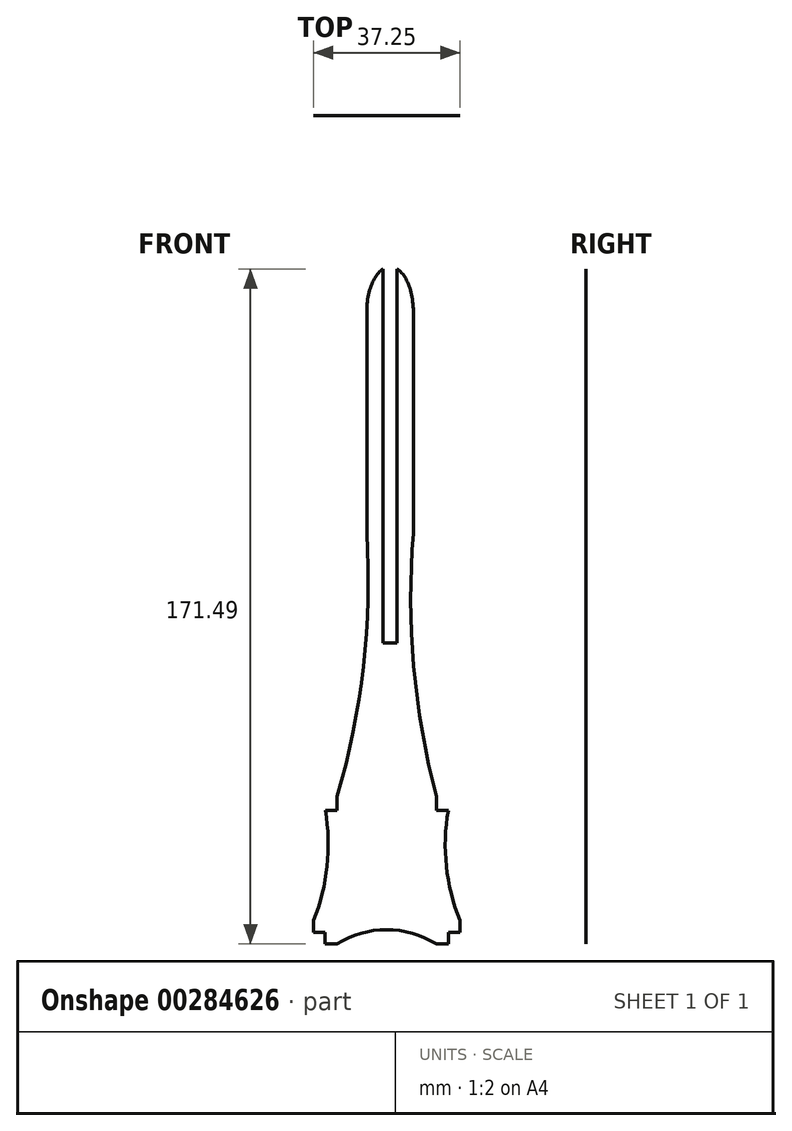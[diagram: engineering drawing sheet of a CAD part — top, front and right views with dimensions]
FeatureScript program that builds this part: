
annotation { "Feature Type Name" : "Feature", "Feature Type Description" : "" }
export const myFeature = defineFeature(function(context is Context, id is Id, definition is map)
    precondition{}
    {
        {
            var Q0;
            Q0=qCreatedBy(makeId("Front.planeOp"),FACE);
            var sketch = newSketch(context, id + "F0", { "sketchPlane" : qUnion([Q0])});
            skLineSegment(sketch, "E0.top", {"start": v(-5.9, 115.39) * mm, "end": v(5.9, 115.39) * mm});
            skLineSegment(sketch, "E0.left", {"start": v(-5.9, 79.83) * mm, "end": v(-5.9, 115.39) * mm});
            skLineSegment(sketch, "E0.right", {"start": v(5.9, 79.83) * mm, "end": v(5.9, 115.39) * mm});
            skEllipse(sketch, "E1", {"center": v(0, 115.39) * mm, "majorRadius": 11.27 * mm, "minorRadius": 5.9 * mm, "majorAxis": v(0, -1)});
            skLineSegment(sketch, "E2.top", {"start": v(-5.9, -45.34) * mm, "end": v(5.9, -45.34) * mm});
            skPoint(sketch, "E3", {"position": v(0, 126.66) * mm});
            skPoint(sketch, "E4.oppositeSnap0", {"position": v(0, -45.34) * mm});
            skLineSegment(sketch, "E4.bottom", {"start": v(-19.47, -7.87) * mm, "end": v(17.78, -7.87) * mm});
            skLineSegment(sketch, "E4.top", {"start": v(-19.47, -45.34) * mm, "end": v(17.78, -45.34) * mm});
            skLineSegment(sketch, "E4.left", {"start": v(-19.47, -7.87) * mm, "end": v(-19.47, -45.34) * mm});
            skLineSegment(sketch, "E4.right", {"start": v(17.78, -7.87) * mm, "end": v(17.78, -45.34) * mm});
            skPoint(sketch, "E5", {"position": v(-0.84, -7.87) * mm});
            skLineSegment(sketch, "E6.left", {"start": v(-19.47, -7.87) * mm, "end": v(-19.47, -10.87) * mm});
            skLineSegment(sketch, "E7.bottom", {"start": v(17.78, -7.87) * mm, "end": v(14.78, -7.87) * mm});
            skLineSegment(sketch, "E7.left", {"start": v(17.78, -7.87) * mm, "end": v(17.78, -10.87) * mm});
            skLineSegment(sketch, "E8.bottom", {"start": v(-19.47, -45.34) * mm, "end": v(-16.52, -45.34) * mm});
            skLineSegment(sketch, "E8.top", {"start": v(-19.47, -42.34) * mm, "end": v(-16.52, -42.34) * mm});
            skLineSegment(sketch, "E8.left", {"start": v(-19.47, -45.34) * mm, "end": v(-19.47, -42.34) * mm});
            skLineSegment(sketch, "E8.right", {"start": v(-16.52, -45.34) * mm, "end": v(-16.52, -42.34) * mm});
            skLineSegment(sketch, "E9.bottom", {"start": v(17.78, -45.34) * mm, "end": v(14.78, -45.34) * mm});
            skLineSegment(sketch, "E9.top", {"start": v(17.78, -42.34) * mm, "end": v(14.78, -42.34) * mm});
            skLineSegment(sketch, "E9.left", {"start": v(17.78, -45.34) * mm, "end": v(17.78, -42.34) * mm});
            skLineSegment(sketch, "E9.right", {"start": v(14.78, -45.34) * mm, "end": v(14.78, -42.34) * mm});
            skLineSegment(sketch, "E10.bottom", {"start": v(-16.47, -7.87) * mm, "end": v(-13.47, -7.87) * mm});
            skLineSegment(sketch, "E10.top", {"start": v(-16.47, -11.37) * mm, "end": v(-13.47, -11.37) * mm});
            skLineSegment(sketch, "E10.left", {"start": v(-16.47, -7.87) * mm, "end": v(-16.47, -11.37) * mm});
            skLineSegment(sketch, "E10.right", {"start": v(-13.47, -7.87) * mm, "end": v(-13.47, -11.37) * mm});
            skLineSegment(sketch, "E11.bottom", {"start": v(14.78, -7.87) * mm, "end": v(11.78, -7.87) * mm});
            skLineSegment(sketch, "E11.top", {"start": v(14.78, -11.37) * mm, "end": v(11.78, -11.37) * mm});
            skLineSegment(sketch, "E11.left", {"start": v(14.78, -7.87) * mm, "end": v(14.78, -11.37) * mm});
            skLineSegment(sketch, "E11.right", {"start": v(11.78, -7.87) * mm, "end": v(11.78, -11.37) * mm});
            skArc(sketch, "E12", {"start": v(-19.47, -39.34) * mm, "mid": v(-16, -25.57) * mm, "end": v(-16.47, -11.37) * mm});
            skArc(sketch, "E13", {"start": v(14.78, -11.37) * mm, "mid": v(14.3, -25.57) * mm, "end": v(17.78, -39.34) * mm});
            skArc(sketch, "E14", {"start": v(11.78, -45.34) * mm, "mid": v(-0.87, -41.7) * mm, "end": v(-13.52, -45.34) * mm});
            skArc(sketch, "E15", {"start": v(-13.47, -7.87) * mm, "mid": v(-6.78, 25.21) * mm, "end": v(-5.9, 58.96) * mm});
            skArc(sketch, "E16", {"start": v(5.9, 58.96) * mm, "mid": v(6, 25.3) * mm, "end": v(11.78, -7.87) * mm});
            skLineSegment(sketch, "E17", {"start": v(-5.9, 79.83) * mm, "end": v(-5.9, 58.96) * mm});
            skLineSegment(sketch, "E18", {"start": v(5.9, 79.83) * mm, "end": v(5.9, 58.96) * mm});
            skLineSegment(sketch, "E19", {"start": v(-1.75, 126.15) * mm, "end": v(-1.75, 31.15) * mm});
            skLineSegment(sketch, "E20", {"start": v(-1.75, 31.15) * mm, "end": v(1.75, 31.15) * mm});
            skLineSegment(sketch, "E21", {"start": v(1.75, 31.15) * mm, "end": v(1.75, 126.15) * mm});
            skPoint(sketch, "E22", {"position": v(0, 31.15) * mm});
            skSolve(sketch);
        }
        {
            var Q0;
            {var subQ0=sQuery(id+"F0.wireOp",EDGE,"E0.top");Q0=makeQuery(id+"F0.imprint","IMPRINT",FACE,{"disambiguationData":[TD([[makeQuery(id+"F0.imprint","IMPRINT",EDGE,{"derivedFrom":subQ0}),1.0]])]});}
            var Q1;
            {var subQ0=sQuery(id+"F0.wireOp",EDGE,"E0.top");Q1=makeQuery(id+"F0.imprint","IMPRINT",FACE,{"disambiguationData":[TD([[makeQuery(id+"F0.imprint","IMPRINT",EDGE,{"derivedFrom":subQ0}),-1.0]])]});}
            var Q2;
            {var subQ1=sQuery(id+"F0.wireOp",EDGE,"E0.left");Q2=makeQuery(id+"F0.imprint","IMPRINT",FACE,{"disambiguationData":[TD([[makeQuery(id+"F0.imprint","IMPRINT",EDGE,{"derivedFrom":subQ1}),-1.0]])]});}
            var Q3;
            {var subQ7=sQuery(id+"F0.wireOp",EDGE,"E8.top");Q3=makeQuery(id+"F0.imprint","IMPRINT",FACE,{"disambiguationData":[TD([[makeQuery(id+"F0.imprint","IMPRINT",EDGE,{"derivedFrom":subQ7}),1.0]])]});}
            extrude(context, id + "F1", {"entities" : qUnion([Q0, Q1, Q2, Q3]), "depth" : 1 / 203.2 * mm});
        }
    });
